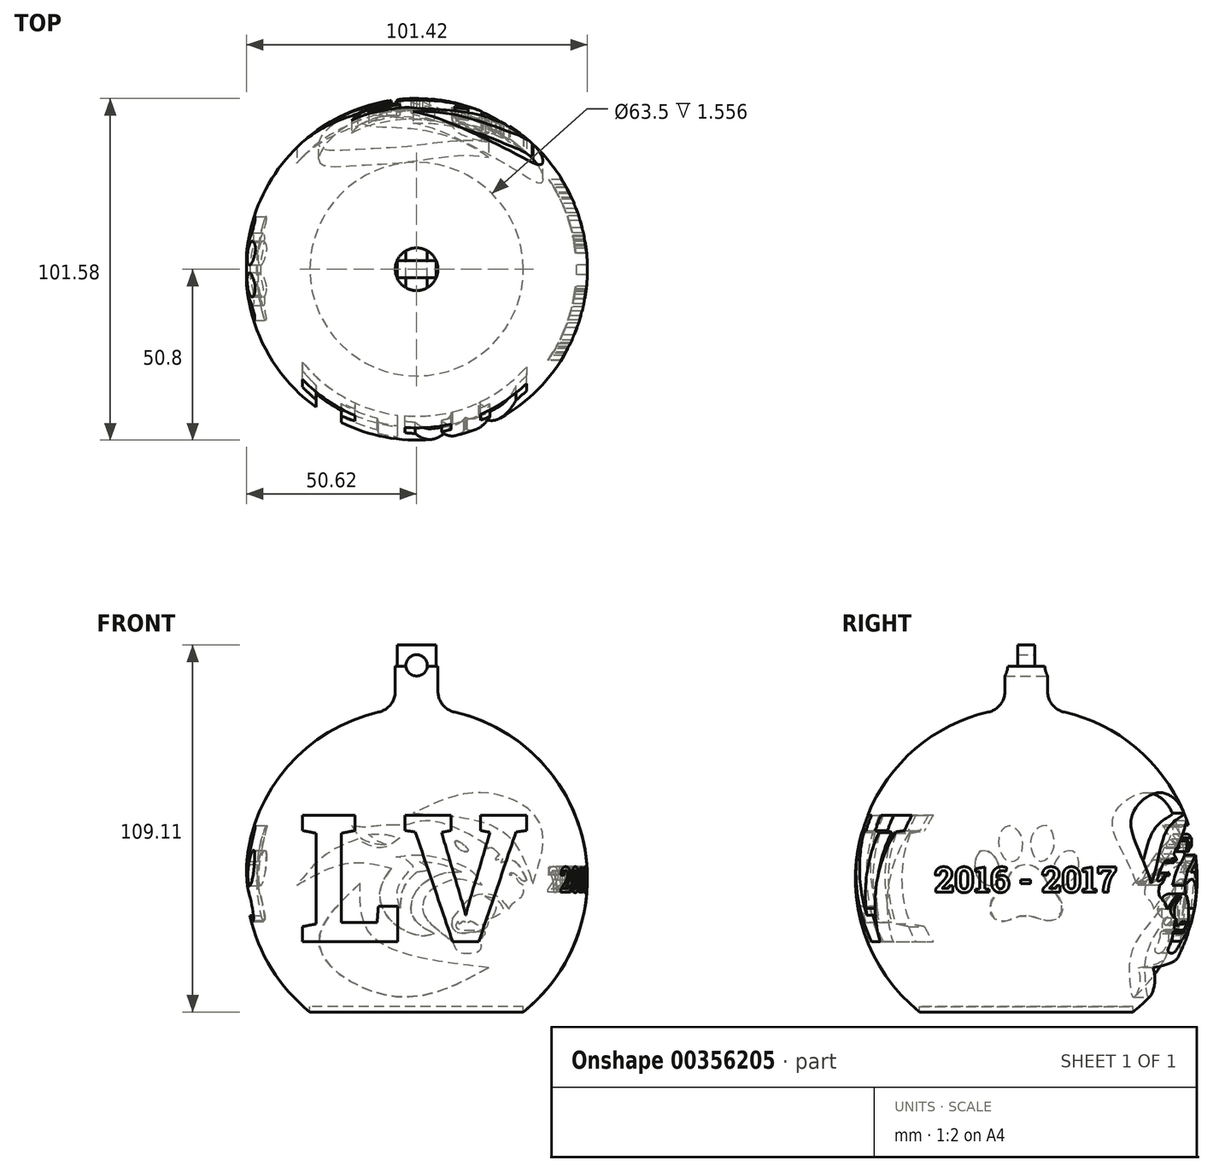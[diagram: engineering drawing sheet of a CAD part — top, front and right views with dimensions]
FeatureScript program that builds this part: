
annotation { "Feature Type Name" : "Feature", "Feature Type Description" : "" }
export const myFeature = defineFeature(function(context is Context, id is Id, definition is map)
    precondition{}
    {
        {
            var Q0;
            Q0=qCreatedBy(makeId("Front.planeOp"),FACE);
            var sketch = newSketch(context, id + "F0", { "sketchPlane" : qUnion([Q0])});
            skArc(sketch, "E0", {"start": v(0, -50.8) * mm, "mid": v(50.48, -5.68) * mm, "end": v(11.29, 49.53) * mm});
            skArc(sketch, "E1.0", {"start": v(0, -44.45) * mm, "mid": v(44.45, 0) * mm, "end": v(0, 44.45) * mm});
            skLineSegment(sketch, "E2.right", {"start": v(6.35, 63.1) * mm, "end": v(6.35, 55.72) * mm});
            skLineSegment(sketch, "E3", {"start": v(0, 76.37) * mm, "end": v(0, -68.75) * mm, "construction": true});
            skPoint(sketch, "E4.visualSharp", {"position": v(-6.35, 50.4) * mm});
            skPoint(sketch, "E5.visualSharp", {"position": v(6.35, 50.4) * mm});
            skArc(sketch, "E5.filletArc", {"start": v(6.35, 55.72) * mm, "mid": v(7.74, 51.76) * mm, "end": v(11.29, 49.53) * mm});
            skLineSegment(sketch, "E6", {"start": v(0, 63.1) * mm, "end": v(6.35, 63.1) * mm});
            skPoint(sketch, "E2.bottom.start.orphan", {"position": v(-6.35, 63.1) * mm});
            skLineSegment(sketch, "E7", {"start": v(0, 63.1) * mm, "end": v(0, 44.45) * mm});
            skLineSegment(sketch, "E8", {"start": v(0, -44.45) * mm, "end": v(0, -50.8) * mm});
            skLineSegment(sketch, "E9", {"start": v(0, 44.45) * mm, "end": v(0, -44.45) * mm});
            skSolve(sketch);
        }
        {
            var Q0;
            Q0 = qSketchRegion(id + "F0", true);
            var Q1;
            Q1=sQuery(id+"F0.wireOp",EDGE,"E3");
            revolve(context, id + "F1", {"entities" : qUnion([Q0]), "axis" : qUnion([Q1]), "revolveType" : RevolveType.FULL});
        }
        {
            var Q0;
            Q0=qCreatedBy(makeId("Front.planeOp"),FACE);
            var sketch = newSketch(context, id + "F2", { "sketchPlane" : qUnion([Q0])});
            skText(sketch, "E10", { "text": "LV", "fontName": "RobotoSlab-Bold.ttf"});
            skPoint(sketch, "E11.1.internal.orphan", {"position": v(0, -32.59) * mm});
            const initialGuessF2  = {"E10": [-0.03536, -0.01878, 1, 0, 0.0381]};
            skSetInitialGuess(sketch, initialGuessF2);
            skSolve(sketch);
        }
        {
            var Q0;
            Q0 = qSketchRegion(id + "F2", true);
            extrude(context, id + "F3", {"entities" : qUnion([Q0]), "operationType" : NewBodyOperationType.REMOVE, "endBound" : BoundingType.THROUGH_ALL, "depth" : 25.4 * mm});
        }
        {
            var Q0;
            Q0=qCreatedBy(makeId("Front.planeOp"),FACE);
            var sketch = newSketch(context, id + "F4", { "sketchPlane" : qUnion([Q0])});
            skFitSpline(sketch, "E12", {"points": [v(-7.52, 3.07) * mm, v(-10.86, -3.34) * mm, v(-8.68, -11.29) * mm, v(0, -16.8) * mm, v(5.3, -16.41) * mm], "startDerivative": vector(-17.93, -24.92) * mm, "endDerivative": vector(23.38, 5.78) * mm});
            skFitSpline(sketch, "E13", {"points": [v(5.3, -16.41) * mm, v(-1.05, -11.5) * mm, v(-1.24, -5.9) * mm, v(2.19, -1.3) * mm, v(8.46, 1.64) * mm, v(13.46, 1.93) * mm], "startDerivative": vector(-34.47, 19.07) * mm, "endDerivative": vector(26.79, -0.85) * mm});
            skFitSpline(sketch, "E14", {"points": [v(13.46, 1.93) * mm, v(7.58, 4.09) * mm, v(0.82, 5.07) * mm], "startDerivative": vector(-11.73, 5.02) * mm, "endDerivative": vector(-13.55, 1.28) * mm});
            skFitSpline(sketch, "E15", {"points": [v(0.82, 5.07) * mm, v(3.76, 2.81) * mm, v(0, 1.93) * mm], "startDerivative": vector(9.25, -5.25) * mm, "endDerivative": vector(-10.81, -1.04) * mm});
            skFitSpline(sketch, "E16", {"points": [v(0, 1.93) * mm, v(-3.8, -2.58) * mm, v(-4.87, -8.85) * mm], "startDerivative": vector(-9.1, -8.43) * mm, "endDerivative": vector(-0.68, -13.1) * mm});
            skFitSpline(sketch, "E17", {"points": [v(-4.87, -8.85) * mm, v(-5.65, -3.17) * mm, v(-0.95, 3.7) * mm], "startDerivative": vector(-4.07, 12.52) * mm, "endDerivative": vector(11.44, 12.57) * mm});
            skFitSpline(sketch, "E18", {"points": [v(-0.95, 3.7) * mm, v(-3.8, 5.95) * mm, v(-6.14, 6.44) * mm], "startDerivative": vector(-5.13, 4.91) * mm, "endDerivative": vector(-5.26, 0.42) * mm});
            skFitSpline(sketch, "E19", {"points": [v(-6.14, 6.44) * mm, v(2.02, 6.98) * mm, v(11.84, 4.6) * mm, v(17.1, 1.57) * mm, v(19.36, -2.04) * mm], "startDerivative": vector(28.47, 4.15) * mm, "endDerivative": vector(10.77, -15.62) * mm});
            skFitSpline(sketch, "E20", {"points": [v(19.36, -2.04) * mm, v(13.84, -0.3) * mm, v(10.23, -0.5) * mm, v(3.25, -4.45) * mm, v(1.68, -8.91) * mm], "startDerivative": vector(-23.11, 8.26) * mm, "endDerivative": vector(-2.4, -19.78) * mm});
            skFitSpline(sketch, "E21", {"points": [v(1.68, -8.91) * mm, v(3.6, -12.75) * mm, v(7.73, -16.41) * mm, v(10.61, -18.63) * mm], "startDerivative": vector(3.92, -14.24) * mm, "endDerivative": vector(9.07, -7.15) * mm});
            skFitSpline(sketch, "E22", {"points": [v(10.61, -18.63) * mm, v(12.36, -21.63) * mm, v(15.99, -22.13) * mm, v(19.11, -21) * mm, v(19.24, -18.63) * mm, v(20.36, -16.41) * mm], "startDerivative": vector(6.19, -16.77) * mm, "endDerivative": vector(8.6, 11.48) * mm});
            skFitSpline(sketch, "E23", {"points": [v(20.36, -16.41) * mm, v(20.36, -15.85) * mm, v(16.28, -15.97) * mm, v(11.94, -15.88) * mm, v(10.49, -14.02) * mm, v(10.66, -12) * mm], "startDerivative": vector(2.26, 6.73) * mm, "endDerivative": vector(2.65, 11.05) * mm});
            skFitSpline(sketch, "E24", {"points": [v(10.66, -12) * mm, v(16.44, -5.46) * mm, v(19.9, -4.48) * mm, v(24.02, -5.36) * mm, v(27.38, -9.07) * mm], "startDerivative": vector(18.52, 24.7) * mm, "endDerivative": vector(12.25, -17.89) * mm});
            skFitSpline(sketch, "E25", {"points": [v(27.38, -9.07) * mm, v(29.18, -6.9) * mm, v(31.55, -4.84) * mm, v(31.7, -1.95) * mm], "startDerivative": vector(4.76, 7) * mm, "endDerivative": vector(-1.3, 9.52) * mm});
            skFitSpline(sketch, "E26", {"points": [v(31.7, -1.95) * mm, v(30.56, -1.2) * mm, v(29.82, 0) * mm, v(28.7, 1.02) * mm, v(27.78, 0.92) * mm], "startDerivative": vector(-5, 2.5) * mm, "endDerivative": vector(-4.32, -1.36) * mm});
            skFitSpline(sketch, "E27", {"points": [v(27.78, 0.92) * mm, v(27.78, 1.53) * mm, v(29.08, 1.44) * mm, v(31.7, -0.7) * mm, v(32.76, -0.47) * mm], "startDerivative": vector(-1.09, 4.3) * mm, "endDerivative": vector(4.47, 2.68) * mm});
            skFitSpline(sketch, "E28", {"points": [v(32.76, -0.47) * mm, v(28.09, 5.49) * mm, v(25.08, 4.83) * mm, v(25.69, 6) * mm, v(23.5, 5.53) * mm, v(24.57, 7.25) * mm], "startDerivative": vector(-11.99, 27.2) * mm, "endDerivative": vector(13.1, 14.95) * mm});
            skFitSpline(sketch, "E29", {"points": [v(24.57, 7.25) * mm, v(21.87, 9.25) * mm, v(21.08, 8.93) * mm, v(20.8, 10.04) * mm], "startDerivative": vector(-6.27, 6.52) * mm, "endDerivative": vector(-0.47, 5.74) * mm});
            skFitSpline(sketch, "E30", {"points": [v(20.8, 10.04) * mm, v(12.28, 14.8) * mm, v(2.35, 17.22) * mm, v(-2.67, 16.08) * mm, v(-6.04, 15.88) * mm], "startDerivative": vector(-26.71, 16.84) * mm, "endDerivative": vector(-18.74, 0.5) * mm});
            skFitSpline(sketch, "E31", {"points": [v(-6.04, 15.88) * mm, v(-9.84, 15.88) * mm, v(-15.48, 15.32) * mm, v(-19.4, 15.88) * mm], "startDerivative": vector(-11.5, 0.58) * mm, "endDerivative": vector(-11.67, 2.69) * mm});
            skFitSpline(sketch, "E32", {"points": [v(-19.4, 15.88) * mm, v(-15.93, 11.68) * mm, v(-8.98, 10.04) * mm], "startDerivative": vector(6.15, -10.41) * mm, "endDerivative": vector(14.52, -1.47) * mm});
            skFitSpline(sketch, "E33", {"points": [v(-8.98, 10.04) * mm, v(-12, 11.45) * mm, v(-14.22, 13.16) * mm], "startDerivative": vector(-6.09, 2.46) * mm, "endDerivative": vector(-4.37, 3.78) * mm});
            skFitSpline(sketch, "E34", {"points": [v(-14.22, 13.16) * mm, v(-9.67, 13.16) * mm, v(-4.94, 12.02) * mm], "startDerivative": vector(9.26, 0.55) * mm, "endDerivative": vector(9.3, -2.81) * mm});
            skFitSpline(sketch, "E35", {"points": [v(-4.94, 12.13) * mm, v(-10.63, 9.17) * mm, v(-17.53, 11.73) * mm], "startDerivative": vector(-11.42, -8.81) * mm, "endDerivative": vector(-13.73, 7.83) * mm});
            skFitSpline(sketch, "E36", {"points": [v(-17.53, 11.73) * mm, v(-26.86, 7.25) * mm, v(-35.62, -1.95) * mm], "startDerivative": vector(-20.4, -7.53) * mm, "endDerivative": vector(-15.87, -19.64) * mm});
            skFitSpline(sketch, "E37", {"points": [v(-35.62, -1.95) * mm, v(-20.35, 4.58) * mm, v(-7.52, 3.07) * mm], "startDerivative": vector(29.1, 16.44) * mm, "endDerivative": vector(27.05, -6.88) * mm});
            skFitSpline(sketch, "E38", {"points": [v(11.63, 11.24) * mm, v(15.36, 8.45) * mm, v(12.85, 8.59) * mm, v(11.63, 11.24) * mm]});
            skFitSpline(sketch, "E39", {"points": [v(20.3, -5.25) * mm, v(23.57, -8.3) * mm, v(22.2, -11.72) * mm], "startDerivative": vector(8.6, -5.45) * mm, "endDerivative": vector(-5.02, -7.52) * mm});
            skFitSpline(sketch, "E40", {"points": [v(22.2, -11.72) * mm, v(24.77, -10.38) * mm, v(25.82, -9.07) * mm], "startDerivative": vector(5.12, 2.15) * mm, "endDerivative": vector(1.96, 3.19) * mm});
            skFitSpline(sketch, "E41", {"points": [v(25.82, -9.07) * mm, v(24.4, -6.77) * mm, v(20.3, -5.25) * mm], "startDerivative": vector(-2.34, 5.77) * mm, "endDerivative": vector(-8.45, 2.02) * mm});
            skFitSpline(sketch, "E42", {"points": [v(21.5, -11.72) * mm, v(18.61, -13.86) * mm, v(15.9, -12.67) * mm, v(14.83, -13.5) * mm, v(14.1, -12.67) * mm, v(12.75, -13.41) * mm, v(12.21, -12.67) * mm], "startDerivative": vector(-11.74, -14.69) * mm, "endDerivative": vector(-3.3, 9.91) * mm});
            skFitSpline(sketch, "E43", {"points": [v(12.21, -12.67) * mm, v(11.82, -14.62) * mm, v(19.79, -15.2) * mm], "startDerivative": vector(-3.34, -6.7) * mm, "endDerivative": vector(16.3, 0.8) * mm});
            skFitSpline(sketch, "E44", {"points": [v(19.79, -15.2) * mm, v(20.99, -14.19) * mm, v(21.5, -11.72) * mm], "startDerivative": vector(3.12, 1.82) * mm, "endDerivative": vector(0.42, 5.02) * mm});
            skPoint(sketch, "E45.0.internal.snap0", {"position": v(34.58, -1.4) * mm});
            skPoint(sketch, "E45.2.internal.snap0", {"position": v(-1.11, 21.26) * mm});
            skFitSpline(sketch, "E45", {"points": [v(34.58, -1.33) * mm, v(25.83, 13.84) * mm, v(-1.11, 19.46) * mm], "startDerivative": vector(-13.75, 37.65) * mm, "endDerivative": vector(-55.92, 3.64) * mm});
            skFitSpline(sketch, "E46", {"points": [v(-1.11, 19.46) * mm, v(19.47, 25.57) * mm, v(36.46, 16.9) * mm, v(34.58, -1.4) * mm], "startDerivative": vector(57.16, 27.46) * mm, "endDerivative": vector(-20.64, -61.9) * mm});
            skFitSpline(sketch, "E47", {"points": [v(-16.81, -1.4) * mm, v(-13.03, -17.32) * mm, v(21.43, -26.48) * mm], "startDerivative": vector(-0.4, -44.27) * mm, "endDerivative": vector(72.23, -8.2) * mm});
            skFitSpline(sketch, "E48", {"points": [v(21.43, -26.48) * mm, v(-6.67, -35.03) * mm, v(-28.91, -20.37) * mm, v(-16.81, -1.4) * mm], "startDerivative": vector(-75.64, -41.44) * mm, "endDerivative": vector(65.12, 61.6) * mm});
            skFitSpline(sketch, "E49", {"points": [v(34.58, -1.4) * mm, v(34.4, -0.8) * mm, v(34.2, -0.25) * mm], "startDerivative": vector(-0.36, 1.18) * mm, "endDerivative": vector(-0.42, 1.11) * mm});
            skSolve(sketch);
        }
        {
            var Q0;
            Q0 = qSketchRegion(id + "F4", true);
            extrude(context, id + "F5", {"entities" : qUnion([Q0]), "operationType" : NewBodyOperationType.REMOVE, "endBound" : BoundingType.THROUGH_ALL, "oppositeDirection" : true, "depth" : 25.4 * mm});
        }
        {
            var Q0;
            Q0=makeQuery(id+"F1.opRevolve","SWEPT_FACE",FACE,{"disambiguationData":[OSD([sQuery(id+"F0.wireOp",EDGE,"E6")])]});
            var sketch = newSketch(context, id + "F6", { "sketchPlane" : qUnion([Q0])});
            skLineSegment(sketch, "E50.bottom", {"start": v(5.81, -2.55) * mm, "end": v(-5.81, -2.55) * mm});
            skLineSegment(sketch, "E50.top", {"start": v(5.81, 2.55) * mm, "end": v(-5.81, 2.55) * mm});
            skLineSegment(sketch, "E50.left", {"start": v(5.81, -2.55) * mm, "end": v(5.81, 2.55) * mm});
            skLineSegment(sketch, "E50.right", {"start": v(-5.81, -2.55) * mm, "end": v(-5.81, 2.55) * mm});
            skPoint(sketch, "E50.middle", {"position": v(0, 0) * mm});
            skSolve(sketch);
        }
        {
            var Q0;
            Q0=qCreatedBy(makeId("Right.planeOp"),FACE);
            var sketch = newSketch(context, id + "F7", { "sketchPlane" : qUnion([Q0])});
            skText(sketch, "E51", { "text": "2016 - 2017", "fontName": "RobotoSlab-Bold.ttf"});
            const initialGuessF7  = {"E51": [-0.02737, -0.00408, 1, 0, 0.00762]};
            skSetInitialGuess(sketch, initialGuessF7);
            skSolve(sketch);
        }
        {
            var Q0;
            Q0=qCreatedBy(makeId("Right.planeOp"),FACE);
            var sketch = newSketch(context, id + "F8", { "sketchPlane" : qUnion([Q0])});
            skFitSpline(sketch, "E52", {"points": [v(9, -4.8) * mm, v(10.6, -7.45) * mm, v(10.13, -10.96) * mm, v(7.22, -12.55) * mm, v(3.64, -11.82) * mm, v(0, -11.03) * mm, v(-3.64, -11.69) * mm, v(-6.49, -12.75) * mm, v(-10.06, -11.36) * mm, v(-10.66, -8.11) * mm, v(-9.93, -5.73) * mm, v(-7.75, -3.28) * mm, v(-5.56, 0) * mm, v(-3.58, 2.94) * mm, v(0, 4.27) * mm, v(3.7, 2.74) * mm, v(5.7, 0) * mm, v(7.02, -2.82) * mm, v(9, -4.8) * mm]});
            skFitSpline(sketch, "E53", {"points": [v(13.9, 8.17) * mm, v(9.86, 6.85) * mm, v(8.01, 1.16) * mm, v(9.93, -2.02) * mm, v(13.97, 0) * mm, v(15.69, 4.73) * mm, v(13.9, 8.17) * mm]});
            skFitSpline(sketch, "E54", {"points": [v(5.9, 15.79) * mm, v(2.38, 14) * mm, v(1.39, 9.03) * mm, v(4.04, 5.13) * mm, v(7.55, 7.64) * mm, v(8.14, 12.54) * mm, v(5.9, 15.79) * mm]});
            skFitSpline(sketch, "E55", {"points": [v(-5.23, 15.72) * mm, v(-8.08, 12.54) * mm, v(-7.68, 7.97) * mm, v(-5.76, 5.4) * mm, v(-3.31, 5.33) * mm, v(-1.46, 7.71) * mm, v(-1.59, 12.87) * mm, v(-5.23, 15.72) * mm]});
            skFitSpline(sketch, "E56", {"points": [v(-13.7, 8.1) * mm, v(-10.73, 7.78) * mm, v(-8.74, 5.33) * mm, v(-7.81, 0.96) * mm, v(-9.93, -2.09) * mm, v(-12.98, -1.03) * mm, v(-15.16, 2.55) * mm, v(-13.7, 8.1) * mm]});
            skSolve(sketch);
        }
        {
            var Q0;
            Q0 = qSketchRegion(id + "F8", true);
            extrude(context, id + "F9", {"entities" : qUnion([Q0]), "operationType" : NewBodyOperationType.REMOVE, "endBound" : BoundingType.THROUGH_ALL, "oppositeDirection" : true, "depth" : 25.4 * mm});
        }
        {
            var Q0;
            Q0 = qSketchRegion(id + "F7", true);
            extrude(context, id + "F10", {"entities" : qUnion([Q0]), "operationType" : NewBodyOperationType.REMOVE, "endBound" : BoundingType.THROUGH_ALL, "depth" : 25.4 * mm});
        }
        {
            var Q0;
            Q0 = qSketchRegion(id + "F6", true);
            extrude(context, id + "F11", {"entities" : qUnion([Q0]), "operationType" : NewBodyOperationType.ADD, "depth" : 6.35 * mm});
        }
        {
            var Q0;
            Q0=makeQuery(id+"F11.opExtrude","SWEPT_FACE",FACE,{"disambiguationData":[OSD([sQuery(id+"F6.wireOp",EDGE,"E50.bottom")])]});
            var sketch = newSketch(context, id + "F12", { "sketchPlane" : qUnion([Q0])});
            skCircle(sketch, "E57", {"center": v(0, 63.42) * mm, "radius": 3.18 * mm});
            skSolve(sketch);
        }
        {
            var Q0;
            Q0 = qSketchRegion(id + "F12", true);
            extrude(context, id + "F13", {"entities" : qUnion([Q0]), "operationType" : NewBodyOperationType.REMOVE, "endBound" : BoundingType.THROUGH_ALL, "depth" : 25.4 * mm, "hasSecondDirection" : true, "secondDirectionBound" : SecondDirectionBoundingType.THROUGH_ALL, "secondDirectionOppositeDirection" : true, "secondDirectionDepth" : 25.4 * mm});
        }
        {
            var Q0;
            Q0=qCreatedBy(makeId("Front.planeOp"),FACE);
            var sketch = newSketch(context, id + "F14", { "sketchPlane" : qUnion([Q0])});
            skArc(sketch, "E58", {"start": v(0, 47.63) * mm, "mid": v(45.6, 13.73) * mm, "end": v(26.3, -39.7) * mm});
            skLineSegment(sketch, "E59", {"start": v(0, 47.63) * mm, "end": v(0, -39.7) * mm});
            skLineSegment(sketch, "E60", {"start": v(0, -39.7) * mm, "end": v(26.3, -39.7) * mm});
            skPoint(sketch, "E61.orphan", {"position": v(0, -47.63) * mm});
            skSolve(sketch);
        }
        {
            var Q0;
            Q0 = qSketchRegion(id + "F14", true);
            var Q1;
            Q1=sQuery(id+"F14.wireOp",EDGE,"E59");
            revolve(context, id + "F15", {"operationType" : NewBodyOperationType.ADD, "entities" : qUnion([Q0]), "axis" : qUnion([Q1]), "revolveType" : RevolveType.FULL});
        }
        {
            var Q0;
            Q0=qCreatedBy(makeId("Top.planeOp"),FACE);
            var sketch = newSketch(context, id + "F16", { "sketchPlane" : qUnion([Q0])});
            skCircle(sketch, "E62", {"center": v(0, 0) * mm, "radius": 31.75 * mm});
            skSolve(sketch);
        }
        {
            var Q0;
            Q0 = qSketchRegion(id + "F16", true);
            extrude(context, id + "F17", {"entities" : qUnion([Q0]), "operationType" : NewBodyOperationType.REMOVE, "oppositeDirection" : true, "depth" : 50.8 * mm});
        }
        {
            var Q0;
            Q0=makeQuery(id+"F17.boolean.opBoolean","COPY",FACE,{"derivedFrom":makeQuery(id+"F17.opExtrude","CAP_FACE",FACE,{"disambiguationData":[OSD([sQuery(id+"F16.wireOp",EDGE,"E62")])],"isStart":true})});
            extrude(context, id + "F18", {"entities" : qUnion([Q0]), "operationType" : NewBodyOperationType.ADD, "depth" : 38.1 * mm});
        }
    });
